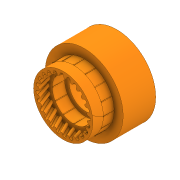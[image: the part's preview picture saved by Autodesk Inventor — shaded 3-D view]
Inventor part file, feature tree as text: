
AUTODESK INVENTOR PART (.ipt)
format: ipt  version: 2020 (Build 240168000, 168)  size: 1,034,752 bytes
history: native  units: in
note: dims shown in document units (in); Inventor stores cm internally (conversion verified against a paired STEP export)
features: sketch x8, extrude x5, chamfer x2, plane x1, sweep x1, projected_geometry x1, other x1
ambient origin geometry x8: Origin, YZ Plane, XZ Plane, XY Plane, X Axis, Y Axis, Z Axis, Center Point
bodies: Solid1 (feature_tree)
feature tree (19):
  extrude  "Extrusion1"  Depth=2.0472in
  extrude  "Extrusion2"  Depth=1.1024in
  chamfer  "Chamfer2"  Distance=0.2756in
  extrude  "Extrusion4"  Depth=0.0157in
  extrude  "Extrusion7"  Depth=0.2756in TaperAngle=0.0deg
  chamfer  "Chamfer4"  Distance=0.0394in
  extrude  "Extrusion8"  Depth=0.0157in
  sketch  "Sketch12"  dims[d39=1.4567in d57=0.0394in d58=0.0in]
  plane  "Work Plane1"
  sketch  "Sketch13"  dims[d59=0.315in d60=0.125in d61=0.0137in d67=0.0157in d68=4.7244in d70=360.0deg d72=0.0394in d73=0.0in d83=0.0591in d84=0.0866in d85=0.0827in d86=0.0827in d87=0.0827in d88=9.4488in d90=360.0deg d92=0.2756in d94=9.4488in d95=0.0827in d96=0.0827in d97=0.0827in d98=360.0deg d99=0.2756in d100=0.0118in d101=1.437in d102=0.0in d103=0.0in d104=0.0in]
  sweep  "Sweep1"
  sketch  "Sketch1"  dims[d0=0.8661in d1=2.0472in]
  sketch  "Sketch2"  dims[d2=0.8563in d3=0.0in d4=1.1024in]
  sketch  "Sketch4"  dims[d5=1.5748in d6=0.2756in d7=0.0in]
  sketch  "Sketch8"  dims[d11=0.2756in d12=0.125in d13=0.0137in d25=0.0157in]
  projected_geometry  "Projected Loop2"
  sketch  "Sketch10"  dims[d26=6.2992in d28=360.0deg d30=0.2756in d31=0.0in]
  sketch  "3D Sketch1"
  other  "Helical Curve1"
